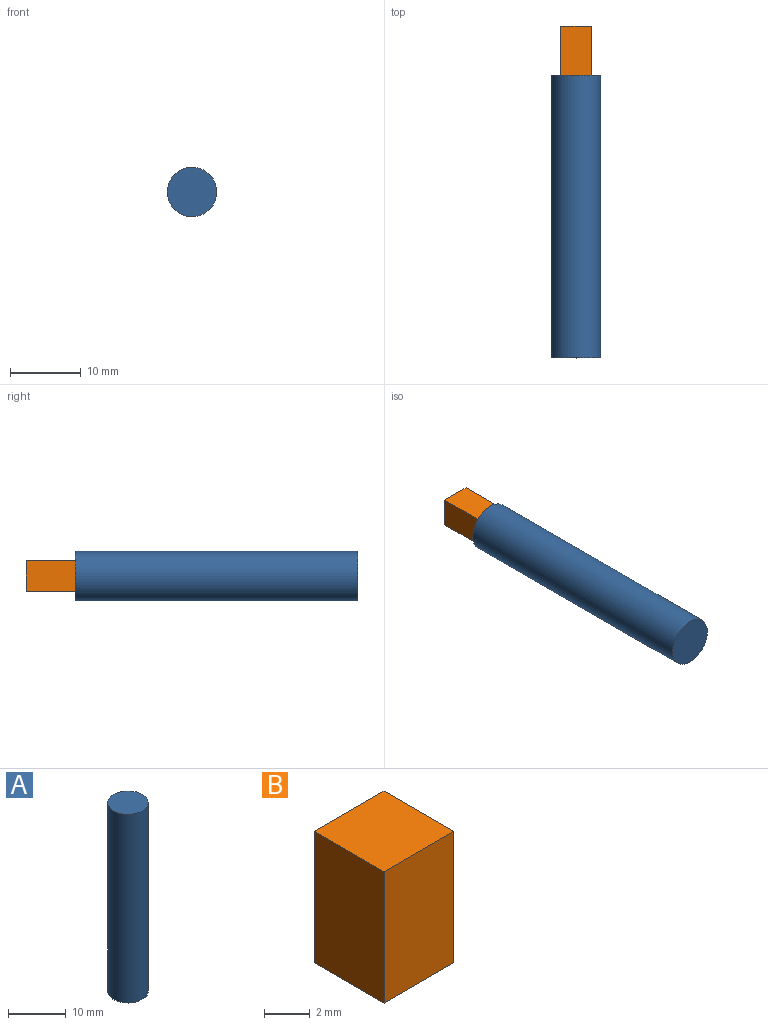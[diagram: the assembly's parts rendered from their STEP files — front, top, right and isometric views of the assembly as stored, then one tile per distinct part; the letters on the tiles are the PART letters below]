
ASSEMBLY  parts=2 mates=1
PART A: 3 faces, bbox 7x7x40 mm
  f0: cylinder r=3.5mm len=40mm, axis (0,0,-1), area 879.6mm2, adj f1,f2
  f1: plane 7x7mm, normal (0,0,1), area 38.5mm2, adj f0
  f2: plane 7x7mm, normal (0,0,-1), area 38.5mm2, adj f0
PART B: 6 faces, bbox 4.3x4.3x7 mm
  f0: plane 7x4.3mm, normal (0,-1,0), area 30.1mm2, adj f1,f3,f4,f5
  f1: plane 7x4.3mm, normal (1,0,0), area 30.1mm2, adj f0,f2,f4,f5
  f2: plane 7x4.3mm, normal (0,1,0), area 30.1mm2, adj f1,f3,f4,f5
  f3: plane 7x4.3mm, normal (-1,0,0), area 30.1mm2, adj f0,f2,f4,f5
  f4: plane 4.3x4.3mm, normal (0,0,1), area 18.5mm2, adj f0,f1,f2,f3
  f5: plane 4.3x4.3mm, normal (0,0,-1), area 18.5mm2, adj f0,f1,f2,f3
PLACE A rot(axis=(0,0.71,0.71),180deg) t=(-21.45,-43.11,15.24)mm
PLACE B rot(axis=(1,0,0),90deg) t=(-21.45,3.89,15.24)mm
MATE revolute B.f4 <-> A.f0  axis (0,-1,0) through (-21.45,-3.11,15.24)mm
